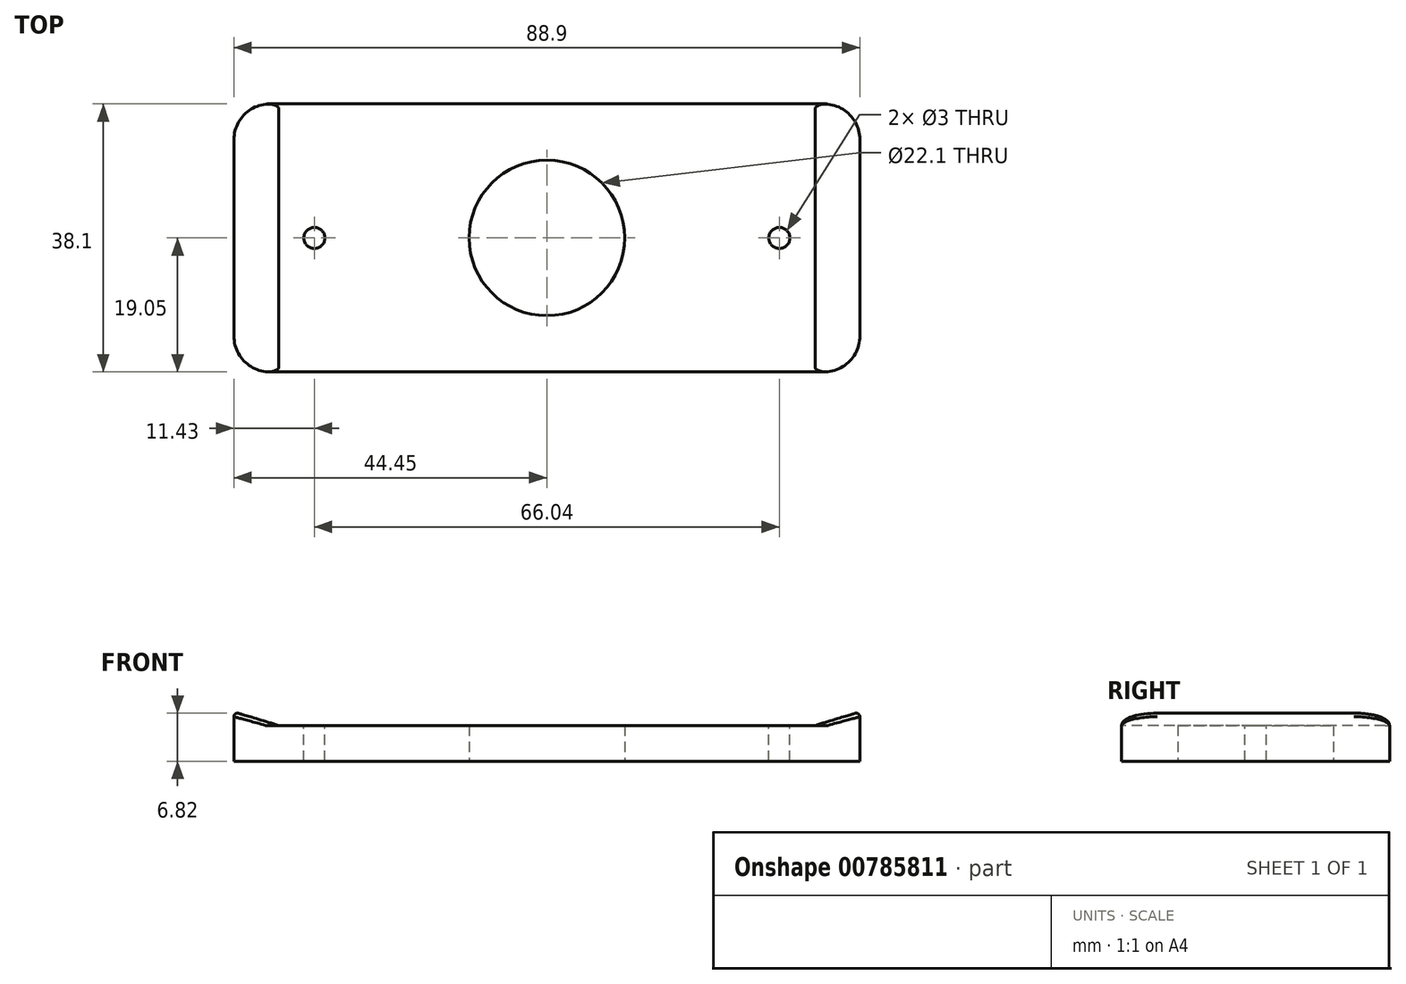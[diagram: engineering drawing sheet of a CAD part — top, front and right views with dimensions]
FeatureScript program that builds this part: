
annotation { "Feature Type Name" : "Feature", "Feature Type Description" : "" }
export const myFeature = defineFeature(function(context is Context, id is Id, definition is map)
    precondition{}
    {
        {
            var Q0;
            Q0=qCreatedBy(makeId("Top.planeOp"),FACE);
            var sketch = newSketch(context, id + "F0", { "sketchPlane" : qUnion([Q0])});
            skCircle(sketch, "E0", {"center": v(0, 0) * mm, "radius": 11.05 * mm});
            skLineSegment(sketch, "E1.bottom", {"start": v(44.45, 19.05) * mm, "end": v(-44.45, 19.05) * mm});
            skLineSegment(sketch, "E1.top", {"start": v(44.45, -19.05) * mm, "end": v(-44.45, -19.05) * mm});
            skLineSegment(sketch, "E1.left", {"start": v(44.45, 19.05) * mm, "end": v(44.45, -19.05) * mm});
            skLineSegment(sketch, "E1.right", {"start": v(-44.45, 19.05) * mm, "end": v(-44.45, -19.05) * mm});
            skSolve(sketch);
        }
        {
            var Q0;
            Q0=makeQuery(id+"F0.imprint","IMPRINT",FACE,{"disambiguationData":[TD([[makeQuery(id+"F0.imprint","IMPRINT",EDGE,{"derivedFrom":sQuery(id+"F0.wireOp",EDGE,"E0")}),-1.0]])]});
            extrude(context, id + "F1", {"entities" : qUnion([Q0]), "depth" : 7 * mm, "offsetDistance" : 25.4 * mm});
        }
        {
            var Q0;
            Q0=makeQuery(id+"F1.opExtrude","SWEPT_FACE",FACE,{"disambiguationData":[OSD([sQuery(id+"F0.wireOp",EDGE,"E1.top")])]});
            var sketch = newSketch(context, id + "F2", { "sketchPlane" : qUnion([Q0])});
            skLineSegment(sketch, "E2", {"start": v(-44.45, 0) * mm, "end": v(-38.1, 0) * mm});
            skLineSegment(sketch, "E3", {"start": v(-38.1, 0) * mm, "end": v(-38.1, 5.08) * mm});
            skLineSegment(sketch, "E4", {"start": v(44.45, 0) * mm, "end": v(38.1, 0) * mm});
            skLineSegment(sketch, "E5", {"start": v(38.1, 0) * mm, "end": v(38.1, 5.08) * mm});
            skLineSegment(sketch, "E6", {"start": v(44.45, 7) * mm, "end": v(38.1, 5.08) * mm});
            skLineSegment(sketch, "E7", {"start": v(-38.1, 5.08) * mm, "end": v(38.1, 5.08) * mm});
            skLineSegment(sketch, "E8", {"start": v(-44.45, 7) * mm, "end": v(-38.1, 5.08) * mm});
            skLineSegment(sketch, "E9", {"start": v(-44.45, 7) * mm, "end": v(44.45, 7) * mm});
            skSolve(sketch);
        }
        {
            var Q0;
            Q0=makeQuery(id+"F2.imprint","IMPRINT",FACE,{"disambiguationData":[TD([[makeQuery(id+"F2.imprint","IMPRINT",EDGE,{"derivedFrom":sQuery(id+"F2.wireOp",EDGE,"E6")}),-1.0]])]});
            extrude(context, id + "F3", {"entities" : qUnion([Q0]), "operationType" : NewBodyOperationType.REMOVE, "oppositeDirection" : true, "depth" : 50.8 * mm, "offsetDistance" : 25.4 * mm});
        }
        {
            var Q0;
            Q0=makeQuery(id+"F1.opExtrude","SWEPT_EDGE",EDGE,{"disambiguationData":[OSD([sQuery(id+"F0.wireOp",EDGE,"E1.top"),sQuery(id+"F0.wireOp",EDGE,"E1.right")])]});
            var Q1;
            Q1=makeQuery(id+"F1.opExtrude","SWEPT_EDGE",EDGE,{"disambiguationData":[OSD([sQuery(id+"F0.wireOp",EDGE,"E1.bottom"),sQuery(id+"F0.wireOp",EDGE,"E1.right")])]});
            var Q2;
            Q2=makeQuery(id+"F1.opExtrude","SWEPT_EDGE",EDGE,{"disambiguationData":[OSD([sQuery(id+"F0.wireOp",EDGE,"E1.bottom"),sQuery(id+"F0.wireOp",EDGE,"E1.left")])]});
            var Q3;
            Q3=makeQuery(id+"F1.opExtrude","SWEPT_EDGE",EDGE,{"disambiguationData":[OSD([sQuery(id+"F0.wireOp",EDGE,"E1.top"),sQuery(id+"F0.wireOp",EDGE,"E1.left")])]});
            fillet(context, id + "F4", {"entities" : qUnion([Q0, Q1, Q2, Q3]), "radius" : 5.08 * mm, "tangentPropagation" : true, "allowEdgeOverflow" : false});
        }
        {
            var Q0;
            {var subQ0=sQuery(id+"F0.wireOp",EDGE,"E1.left");Q0=makeQuery(id+"F3.boolean.opBoolean","MERGE",EDGE,{"derivedFrom":[makeQuery(id+"F1.opExtrude","CAP_EDGE",EDGE,{"disambiguationData":[OSD([subQ0])],"isStart":false}),makeQuery(id+"F3.opExtrude","SWEPT_EDGE",EDGE,{"disambiguationData":[OSD([sQuery(id+"F0.wireOp",EDGE,"E1.top"),subQ0,sQuery(id+"F2.wireOp",EDGE,"E6"),sQuery(id+"F2.wireOp",EDGE,"E9")])]})]});}
            var Q1;
            {var subQ0=sQuery(id+"F0.wireOp",EDGE,"E1.right");Q1=makeQuery(id+"F3.boolean.opBoolean","MERGE",EDGE,{"derivedFrom":[makeQuery(id+"F1.opExtrude","CAP_EDGE",EDGE,{"disambiguationData":[OSD([subQ0])],"isStart":false}),makeQuery(id+"F3.opExtrude","SWEPT_EDGE",EDGE,{"disambiguationData":[OSD([sQuery(id+"F0.wireOp",EDGE,"E1.top"),subQ0,sQuery(id+"F2.wireOp",EDGE,"E8"),sQuery(id+"F2.wireOp",EDGE,"E9")])]})]});}
            fillet(context, id + "F5", {"entities" : qUnion([Q0, Q1]), "radius" : 0.5 * mm, "tangentPropagation" : true, "allowEdgeOverflow" : false});
        }
        {
            var Q0;
            Q0=makeQuery(id+"F3.boolean.opBoolean","COPY",FACE,{"derivedFrom":makeQuery(id+"F3.opExtrude","SWEPT_FACE",FACE,{"disambiguationData":[OSD([sQuery(id+"F2.wireOp",EDGE,"E7")])]})});
            var sketch = newSketch(context, id + "F6", { "sketchPlane" : qUnion([Q0])});
            skLineSegment(sketch, "E10", {"start": v(38.1, 0) * mm, "end": v(33.02, 0) * mm});
            skLineSegment(sketch, "E11", {"start": v(-38.1, 0) * mm, "end": v(-33.02, 0) * mm});
            skCircle(sketch, "E12", {"center": v(-33.02, 0) * mm, "radius": 1.5 * mm});
            skCircle(sketch, "E13", {"center": v(33.02, 0) * mm, "radius": 1.5 * mm});
            skSolve(sketch);
        }
        {
            var Q0;
            Q0=makeQuery(id+"F6.imprint","IMPRINT",FACE,{"disambiguationData":[TD([[makeQuery(id+"F6.imprint","IMPRINT",EDGE,{"derivedFrom":sQuery(id+"F6.wireOp",EDGE,"E13")}),1.0]])]});
            var Q1;
            Q1=makeQuery(id+"F6.imprint","IMPRINT",FACE,{"disambiguationData":[TD([[makeQuery(id+"F6.imprint","IMPRINT",EDGE,{"derivedFrom":sQuery(id+"F6.wireOp",EDGE,"E12")}),1.0]])]});
            extrude(context, id + "F7", {"entities" : qUnion([Q0, Q1]), "operationType" : NewBodyOperationType.REMOVE, "oppositeDirection" : true, "depth" : 25.4 * mm, "offsetDistance" : 25.4 * mm});
        }
    });
